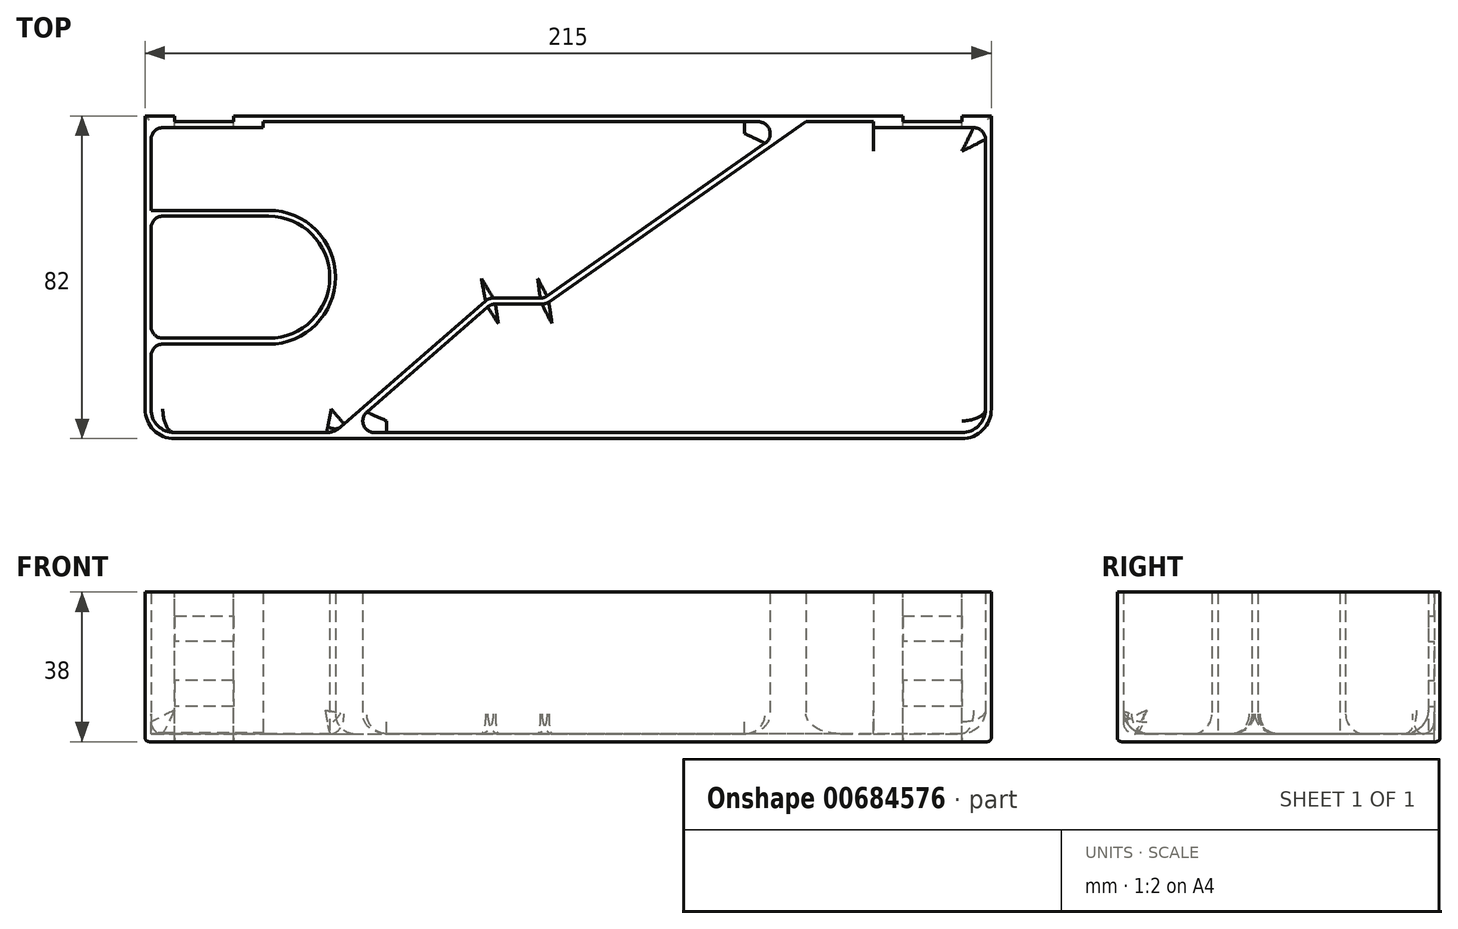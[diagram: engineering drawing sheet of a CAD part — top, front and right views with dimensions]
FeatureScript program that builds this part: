
annotation { "Feature Type Name" : "Feature", "Feature Type Description" : "" }
export const myFeature = defineFeature(function(context is Context, id is Id, definition is map)
    precondition{}
    {
        {
            var Q0;
            Q0=qCreatedBy(makeId("Top.planeOp"),FACE);
            var sketch = newSketch(context, id + "F0", { "sketchPlane" : qUnion([Q0])});
            skLineSegment(sketch, "E0.bottom", {"start": v(0, 0) * mm, "end": v(215, 0) * mm});
            skLineSegment(sketch, "E0.top", {"start": v(0, 82) * mm, "end": v(215, 82) * mm});
            skLineSegment(sketch, "E0.left", {"start": v(0, 0) * mm, "end": v(0, 82) * mm});
            skLineSegment(sketch, "E0.right", {"start": v(215, 0) * mm, "end": v(215, 82) * mm});
            skSolve(sketch);
        }
        {
            var Q0;
            Q0=makeQuery(id+"F0.imprint","IMPRINT",FACE,{"disambiguationData":[TD([[makeQuery(id+"F0.imprint","IMPRINT",EDGE,{"derivedFrom":sQuery(id+"F0.wireOp",EDGE,"E0.bottom")}),1.0]])]});
            extrude(context, id + "F1", {"entities" : qUnion([Q0]), "depth" : 2 * mm});
        }
        {
            var Q0;
            Q0=makeQuery(id+"F1.opExtrude","CAP_FACE",FACE,{"disambiguationData":[OSD([sQuery(id+"F0.wireOp",EDGE,"E0.bottom"),sQuery(id+"F0.wireOp",EDGE,"E0.top"),sQuery(id+"F0.wireOp",EDGE,"E0.left"),sQuery(id+"F0.wireOp",EDGE,"E0.right")])],"isStart":false});
            var sketch = newSketch(context, id + "F2", { "sketchPlane" : qUnion([Q0])});
            skLineSegment(sketch, "E1", {"start": v(1.5, 79) * mm, "end": v(30, 79) * mm});
            skLineSegment(sketch, "E2", {"start": v(30, 79) * mm, "end": v(30, 80.5) * mm});
            skLineSegment(sketch, "E3", {"start": v(30, 80.5) * mm, "end": v(185, 80.5) * mm});
            skLineSegment(sketch, "E4", {"start": v(185, 80.5) * mm, "end": v(185, 79) * mm});
            skLineSegment(sketch, "E5", {"start": v(185, 79) * mm, "end": v(213.5, 79) * mm});
            skLineSegment(sketch, "E6", {"start": v(213.5, 79) * mm, "end": v(213.5, 1.5) * mm});
            skLineSegment(sketch, "E7", {"start": v(213.5, 1.5) * mm, "end": v(1.5, 1.5) * mm});
            skLineSegment(sketch, "E8", {"start": v(1.5, 1.5) * mm, "end": v(1.5, 79) * mm});
            skSolve(sketch);
        }
        {
            var Q0;
            Q0=makeQuery(id+"F2.imprint","IMPRINT",FACE,{"disambiguationData":[TD([[makeQuery(id+"F2.imprint","IMPRINT",EDGE,{"derivedFrom":sQuery(id+"F2.wireOp",EDGE,"E1")}),1.0]])]});
            extrude(context, id + "F3", {"entities" : qUnion([Q0]), "operationType" : NewBodyOperationType.ADD, "depth" : 36 * mm});
        }
        {
            var Q0;
            Q0=makeQuery(id+"F1.opExtrude","CAP_FACE",FACE,{"disambiguationData":[OSD([sQuery(id+"F0.wireOp",EDGE,"E0.bottom"),sQuery(id+"F0.wireOp",EDGE,"E0.top"),sQuery(id+"F0.wireOp",EDGE,"E0.left"),sQuery(id+"F0.wireOp",EDGE,"E0.right")])],"isStart":false});
            var sketch = newSketch(context, id + "F4", { "sketchPlane" : qUnion([Q0])});
            skLineSegment(sketch, "E9", {"start": v(1.5, 58) * mm, "end": v(31.4, 58) * mm});
            skArc(sketch, "E10", {"start": v(31.4, 58) * mm, "mid": v(48.4, 41) * mm, "end": v(31.4, 24) * mm});
            skLineSegment(sketch, "E11", {"start": v(31.4, 24) * mm, "end": v(1.5, 24) * mm});
            skLineSegment(sketch, "E12", {"start": v(1.5, 24) * mm, "end": v(1.5, 25.5) * mm});
            skLineSegment(sketch, "E13", {"start": v(1.5, 25.5) * mm, "end": v(31.4, 25.5) * mm});
            skArc(sketch, "E14", {"start": v(31.4, 25.5) * mm, "mid": v(46.9, 41) * mm, "end": v(31.4, 56.5) * mm});
            skLineSegment(sketch, "E15", {"start": v(31.4, 56.5) * mm, "end": v(1.5, 56.5) * mm});
            skLineSegment(sketch, "E16", {"start": v(1.5, 56.5) * mm, "end": v(1.5, 58) * mm});
            skLineSegment(sketch, "E17", {"start": v(48, 1.5) * mm, "end": v(87.33, 35.69) * mm});
            skLineSegment(sketch, "E18", {"start": v(87.33, 35.69) * mm, "end": v(101.33, 35.69) * mm});
            skLineSegment(sketch, "E19", {"start": v(101.33, 35.69) * mm, "end": v(165.33, 80.5) * mm});
            skLineSegment(sketch, "E20", {"start": v(165.33, 80.5) * mm, "end": v(167.94, 80.5) * mm});
            skLineSegment(sketch, "E21", {"start": v(167.94, 80.5) * mm, "end": v(101.8, 34.19) * mm});
            skLineSegment(sketch, "E22", {"start": v(101.8, 34.19) * mm, "end": v(87.89, 34.19) * mm});
            skLineSegment(sketch, "E23", {"start": v(87.89, 34.19) * mm, "end": v(50.29, 1.5) * mm});
            skLineSegment(sketch, "E24", {"start": v(50.29, 1.5) * mm, "end": v(48, 1.5) * mm});
            skSolve(sketch);
        }
        {
            var Q0;
            Q0=makeQuery(id+"F4.imprint","IMPRINT",FACE,{"disambiguationData":[TD([[makeQuery(id+"F4.imprint","IMPRINT",EDGE,{"derivedFrom":sQuery(id+"F4.wireOp",EDGE,"E9")}),-1.0]])]});
            var Q1;
            Q1=makeQuery(id+"F4.imprint","IMPRINT",FACE,{"disambiguationData":[TD([[makeQuery(id+"F4.imprint","IMPRINT",EDGE,{"derivedFrom":sQuery(id+"F4.wireOp",EDGE,"E17")}),-1.0]])]});
            extrude(context, id + "F5", {"entities" : qUnion([Q0, Q1]), "operationType" : NewBodyOperationType.ADD, "depth" : 36 * mm});
        }
        {
            var Q0;
            Q0=makeQuery(id+"F1.opExtrude","CAP_EDGE",EDGE,{"disambiguationData":[OSD([sQuery(id+"F0.wireOp",EDGE,"E0.bottom")])],"isStart":true});
            var Q1;
            Q1=makeQuery(id+"F1.opExtrude","CAP_EDGE",EDGE,{"disambiguationData":[OSD([sQuery(id+"F0.wireOp",EDGE,"E0.right")])],"isStart":true});
            var Q2;
            Q2=makeQuery(id+"F1.opExtrude","CAP_EDGE",EDGE,{"disambiguationData":[OSD([sQuery(id+"F0.wireOp",EDGE,"E0.top")])],"isStart":true});
            var Q3;
            Q3=makeQuery(id+"F1.opExtrude","CAP_EDGE",EDGE,{"disambiguationData":[OSD([sQuery(id+"F0.wireOp",EDGE,"E0.left")])],"isStart":true});
            fillet(context, id + "F6", {"entities" : qUnion([Q0, Q1, Q2, Q3]), "radius" : 1 * mm, "tangentPropagation" : true, "allowEdgeOverflow" : false});
        }
        {
            var Q0;
            {var subQ0=sQuery(id+"F2.wireOp",EDGE,"E7");Q0=makeQuery(id+"F5.boolean.opBoolean","SPLIT",EDGE,{"disambiguationData":[TD([makeQuery(id+"F3.opExtrude","SWEPT_FACE",FACE,{"disambiguationData":[OSD([sQuery(id+"F2.wireOp",EDGE,"E6")])]})])],"derivedFrom":makeQuery(id+"F3.opExtrude","CAP_EDGE",EDGE,{"disambiguationData":[OSD([subQ0])],"isStart":true})});}
            var Q1;
            Q1=makeQuery(id+"F5.opExtrude","CAP_EDGE",EDGE,{"disambiguationData":[OSD([sQuery(id+"F4.wireOp",EDGE,"E23")])],"isStart":true});
            var Q2;
            Q2=makeQuery(id+"F5.opExtrude","CAP_EDGE",EDGE,{"disambiguationData":[OSD([sQuery(id+"F4.wireOp",EDGE,"E21")])],"isStart":true});
            var Q3;
            Q3=makeQuery(id+"F5.opExtrude","CAP_EDGE",EDGE,{"disambiguationData":[OSD([sQuery(id+"F4.wireOp",EDGE,"E22")])],"isStart":true});
            var Q4;
            {var subQ0=sQuery(id+"F2.wireOp",EDGE,"E3");Q4=makeQuery(id+"F5.boolean.opBoolean","SPLIT",EDGE,{"disambiguationData":[TD([makeQuery(id+"F3.opExtrude","SWEPT_FACE",FACE,{"disambiguationData":[OSD([sQuery(id+"F2.wireOp",EDGE,"E4")])]})])],"derivedFrom":makeQuery(id+"F3.opExtrude","CAP_EDGE",EDGE,{"disambiguationData":[OSD([subQ0])],"isStart":true})});}
            var Q5;
            Q5=makeQuery(id+"F3.opExtrude","CAP_EDGE",EDGE,{"disambiguationData":[OSD([sQuery(id+"F2.wireOp",EDGE,"E6")])],"isStart":true});
            var Q6;
            {var subQ0=sQuery(id+"F2.wireOp",EDGE,"E3");Q6=makeQuery(id+"F5.boolean.opBoolean","SPLIT",EDGE,{"disambiguationData":[TD([makeQuery(id+"F3.opExtrude","SWEPT_FACE",FACE,{"disambiguationData":[OSD([sQuery(id+"F2.wireOp",EDGE,"E2")])]})])],"derivedFrom":makeQuery(id+"F3.opExtrude","CAP_EDGE",EDGE,{"disambiguationData":[OSD([subQ0])],"isStart":true})});}
            var Q7;
            Q7=makeQuery(id+"F5.opExtrude","CAP_EDGE",EDGE,{"disambiguationData":[OSD([sQuery(id+"F4.wireOp",EDGE,"E19")])],"isStart":true});
            var Q8;
            Q8=makeQuery(id+"F5.opExtrude","CAP_EDGE",EDGE,{"disambiguationData":[OSD([sQuery(id+"F4.wireOp",EDGE,"E18")])],"isStart":true});
            var Q9;
            Q9=makeQuery(id+"F5.opExtrude","CAP_EDGE",EDGE,{"disambiguationData":[OSD([sQuery(id+"F4.wireOp",EDGE,"E17")])],"isStart":true});
            var Q10;
            {var subQ0=sQuery(id+"F2.wireOp",EDGE,"E8");Q10=makeQuery(id+"F5.boolean.opBoolean","SPLIT",EDGE,{"disambiguationData":[TD([makeQuery(id+"F3.opExtrude","SWEPT_FACE",FACE,{"disambiguationData":[OSD([sQuery(id+"F2.wireOp",EDGE,"E1")])]})])],"derivedFrom":makeQuery(id+"F3.opExtrude","CAP_EDGE",EDGE,{"disambiguationData":[OSD([subQ0])],"isStart":true})});}
            var Q11;
            Q11=makeQuery(id+"F5.opExtrude","CAP_EDGE",EDGE,{"disambiguationData":[OSD([sQuery(id+"F4.wireOp",EDGE,"E10")])],"isStart":true});
            var Q12;
            {var subQ0=sQuery(id+"F2.wireOp",EDGE,"E8");Q12=makeQuery(id+"F5.boolean.opBoolean","SPLIT",EDGE,{"disambiguationData":[TD([makeQuery(id+"F3.opExtrude","SWEPT_FACE",FACE,{"disambiguationData":[OSD([sQuery(id+"F2.wireOp",EDGE,"E7")])]})])],"derivedFrom":makeQuery(id+"F3.opExtrude","CAP_EDGE",EDGE,{"disambiguationData":[OSD([subQ0])],"isStart":true})});}
            var Q13;
            {var subQ0=sQuery(id+"F2.wireOp",EDGE,"E8");Q13=makeQuery(id+"F5.boolean.opBoolean","SPLIT",EDGE,{"disambiguationData":[TD([makeQuery(id+"F5.opExtrude","SWEPT_FACE",FACE,{"disambiguationData":[OSD([sQuery(id+"F4.wireOp",EDGE,"E13")])]})])],"derivedFrom":makeQuery(id+"F3.opExtrude","CAP_EDGE",EDGE,{"disambiguationData":[OSD([subQ0])],"isStart":true})});}
            var Q14;
            Q14=makeQuery(id+"F5.opExtrude","CAP_EDGE",EDGE,{"disambiguationData":[OSD([sQuery(id+"F4.wireOp",EDGE,"E15")])],"isStart":true});
            var Q15;
            {var subQ0=sQuery(id+"F2.wireOp",EDGE,"E7");Q15=makeQuery(id+"F5.boolean.opBoolean","SPLIT",EDGE,{"disambiguationData":[TD([makeQuery(id+"F3.opExtrude","SWEPT_FACE",FACE,{"disambiguationData":[OSD([sQuery(id+"F2.wireOp",EDGE,"E8")])]})])],"derivedFrom":makeQuery(id+"F3.opExtrude","CAP_EDGE",EDGE,{"disambiguationData":[OSD([subQ0])],"isStart":true})});}
            fillet(context, id + "F7", {"entities" : qUnion([Q0, Q1, Q2, Q3, Q4, Q5, Q6, Q7, Q8, Q9, Q10, Q11, Q12, Q13, Q14, Q15]), "radius" : 5 * mm, "tangentPropagation" : true, "allowEdgeOverflow" : false});
        }
        {
            var Q0;
            Q0=makeQuery(id+"F5.opExtrude","SWEPT_EDGE",EDGE,{"disambiguationData":[OSD([sQuery(id+"F2.wireOp",EDGE,"E7"),sQuery(id+"F4.wireOp",EDGE,"E17"),sQuery(id+"F4.wireOp",EDGE,"E24")])]});
            var Q1;
            Q1=makeQuery(id+"F5.opExtrude","SWEPT_EDGE",EDGE,{"disambiguationData":[OSD([sQuery(id+"F4.wireOp",EDGE,"E17"),sQuery(id+"F4.wireOp",EDGE,"E18")])]});
            var Q2;
            Q2=makeQuery(id+"F5.opExtrude","SWEPT_EDGE",EDGE,{"disambiguationData":[OSD([sQuery(id+"F4.wireOp",EDGE,"E18"),sQuery(id+"F4.wireOp",EDGE,"E19")])]});
            var Q3;
            Q3=makeQuery(id+"F5.opExtrude","SWEPT_EDGE",EDGE,{"disambiguationData":[OSD([sQuery(id+"F2.wireOp",EDGE,"E8"),sQuery(id+"F4.wireOp",EDGE,"E12"),sQuery(id+"F4.wireOp",EDGE,"E13")])]});
            var Q4;
            Q4=makeQuery(id+"F5.opExtrude","SWEPT_EDGE",EDGE,{"disambiguationData":[OSD([sQuery(id+"F2.wireOp",EDGE,"E8"),sQuery(id+"F4.wireOp",EDGE,"E9"),sQuery(id+"F4.wireOp",EDGE,"E16")])]});
            var Q5;
            Q5=makeQuery(id+"F5.opExtrude","SWEPT_EDGE",EDGE,{"disambiguationData":[OSD([sQuery(id+"F2.wireOp",EDGE,"E8"),sQuery(id+"F4.wireOp",EDGE,"E15"),sQuery(id+"F4.wireOp",EDGE,"E16")])]});
            var Q6;
            Q6=makeQuery(id+"F3.opExtrude","SWEPT_EDGE",EDGE,{"disambiguationData":[OSD([sQuery(id+"F2.wireOp",EDGE,"E1"),sQuery(id+"F2.wireOp",EDGE,"E8")])]});
            var Q7;
            Q7=makeQuery(id+"F5.opExtrude","SWEPT_EDGE",EDGE,{"disambiguationData":[OSD([sQuery(id+"F2.wireOp",EDGE,"E3"),sQuery(id+"F4.wireOp",EDGE,"E20"),sQuery(id+"F4.wireOp",EDGE,"E21")])]});
            var Q8;
            Q8=makeQuery(id+"F5.opExtrude","SWEPT_EDGE",EDGE,{"disambiguationData":[OSD([sQuery(id+"F2.wireOp",EDGE,"E3"),sQuery(id+"F4.wireOp",EDGE,"E19"),sQuery(id+"F4.wireOp",EDGE,"E20")])]});
            var Q9;
            Q9=makeQuery(id+"F3.opExtrude","SWEPT_EDGE",EDGE,{"disambiguationData":[OSD([sQuery(id+"F2.wireOp",EDGE,"E5"),sQuery(id+"F2.wireOp",EDGE,"E6")])]});
            var Q10;
            Q10=makeQuery(id+"F5.opExtrude","SWEPT_EDGE",EDGE,{"disambiguationData":[OSD([sQuery(id+"F2.wireOp",EDGE,"E7"),sQuery(id+"F4.wireOp",EDGE,"E23"),sQuery(id+"F4.wireOp",EDGE,"E24")])]});
            var Q11;
            Q11=makeQuery(id+"F5.opExtrude","SWEPT_EDGE",EDGE,{"disambiguationData":[OSD([sQuery(id+"F4.wireOp",EDGE,"E22"),sQuery(id+"F4.wireOp",EDGE,"E23")])]});
            var Q12;
            Q12=makeQuery(id+"F5.opExtrude","SWEPT_EDGE",EDGE,{"disambiguationData":[OSD([sQuery(id+"F4.wireOp",EDGE,"E21"),sQuery(id+"F4.wireOp",EDGE,"E22")])]});
            var Q13;
            Q13=makeQuery(id+"F5.opExtrude","SWEPT_EDGE",EDGE,{"disambiguationData":[OSD([sQuery(id+"F2.wireOp",EDGE,"E8"),sQuery(id+"F4.wireOp",EDGE,"E11"),sQuery(id+"F4.wireOp",EDGE,"E12")])]});
            fillet(context, id + "F8", {"entities" : qUnion([Q0, Q1, Q2, Q3, Q4, Q5, Q6, Q7, Q8, Q9, Q10, Q11, Q12, Q13]), "radius" : 3 * mm, "tangentPropagation" : true, "allowEdgeOverflow" : false});
        }
        {
            var Q0;
            Q0=makeQuery(id+"F3.opExtrude","SWEPT_EDGE",EDGE,{"disambiguationData":[OSD([sQuery(id+"F2.wireOp",EDGE,"E7"),sQuery(id+"F2.wireOp",EDGE,"E8")])]});
            var Q1;
            Q1=makeQuery(id+"F3.opExtrude","SWEPT_EDGE",EDGE,{"disambiguationData":[OSD([sQuery(id+"F2.wireOp",EDGE,"E6"),sQuery(id+"F2.wireOp",EDGE,"E7")])]});
            fillet(context, id + "F9", {"entities" : qUnion([Q0, Q1]), "radius" : 6 * mm, "tangentPropagation" : true, "allowEdgeOverflow" : false});
        }
        {
            var Q0;
            {var subQ0=sQuery(id+"F0.wireOp",EDGE,"E0.left");var subQ1=sQuery(id+"F0.wireOp",EDGE,"E0.bottom");Q0=makeQuery(id+"F3.boolean.opBoolean","MERGE",EDGE,{"derivedFrom":[makeQuery(id+"F1.opExtrude","SWEPT_EDGE",EDGE,{"disambiguationData":[OSD([subQ1,subQ0])]}),makeQuery(id+"F3.opExtrude","SWEPT_EDGE",EDGE,{"disambiguationData":[OSD([subQ1,subQ0])]})]});}
            var Q1;
            {var subQ0=sQuery(id+"F0.wireOp",EDGE,"E0.right");var subQ1=sQuery(id+"F0.wireOp",EDGE,"E0.bottom");Q1=makeQuery(id+"F3.boolean.opBoolean","MERGE",EDGE,{"derivedFrom":[makeQuery(id+"F1.opExtrude","SWEPT_EDGE",EDGE,{"disambiguationData":[OSD([subQ1,subQ0])]}),makeQuery(id+"F3.opExtrude","SWEPT_EDGE",EDGE,{"disambiguationData":[OSD([subQ1,subQ0])]})]});}
            fillet(context, id + "F10", {"entities" : qUnion([Q0, Q1]), "radius" : 7.5 * mm, "tangentPropagation" : true, "allowEdgeOverflow" : false});
        }
        {
            var Q0;
            Q0=makeQuery(id+"F5.boolean.opBoolean","MERGE",FACE,{"derivedFrom":[makeQuery(id+"F3.opExtrude","CAP_FACE",FACE,{"disambiguationData":[OSD([sQuery(id+"F0.wireOp",EDGE,"E0.bottom"),sQuery(id+"F0.wireOp",EDGE,"E0.top"),sQuery(id+"F0.wireOp",EDGE,"E0.left"),sQuery(id+"F0.wireOp",EDGE,"E0.right"),sQuery(id+"F2.wireOp",EDGE,"E1"),sQuery(id+"F2.wireOp",EDGE,"E2"),sQuery(id+"F2.wireOp",EDGE,"E3"),sQuery(id+"F2.wireOp",EDGE,"E4"),sQuery(id+"F2.wireOp",EDGE,"E5"),sQuery(id+"F2.wireOp",EDGE,"E6"),sQuery(id+"F2.wireOp",EDGE,"E7"),sQuery(id+"F2.wireOp",EDGE,"E8")])],"isStart":false}),makeQuery(id+"F5.opExtrude","CAP_FACE",FACE,{"disambiguationData":[OSD([sQuery(id+"F4.wireOp",EDGE,"E9"),sQuery(id+"F4.wireOp",EDGE,"E10"),sQuery(id+"F4.wireOp",EDGE,"E11"),sQuery(id+"F4.wireOp",EDGE,"E12"),sQuery(id+"F4.wireOp",EDGE,"E13"),sQuery(id+"F4.wireOp",EDGE,"E14"),sQuery(id+"F4.wireOp",EDGE,"E15"),sQuery(id+"F4.wireOp",EDGE,"E16")])],"isStart":false}),makeQuery(id+"F5.opExtrude","CAP_FACE",FACE,{"disambiguationData":[OSD([sQuery(id+"F4.wireOp",EDGE,"E17"),sQuery(id+"F4.wireOp",EDGE,"E18"),sQuery(id+"F4.wireOp",EDGE,"E19"),sQuery(id+"F4.wireOp",EDGE,"E20"),sQuery(id+"F4.wireOp",EDGE,"E21"),sQuery(id+"F4.wireOp",EDGE,"E22"),sQuery(id+"F4.wireOp",EDGE,"E23"),sQuery(id+"F4.wireOp",EDGE,"E24")])],"isStart":false})]});
            var sketch = newSketch(context, id + "F11", { "sketchPlane" : qUnion([Q0])});
            skLineSegment(sketch, "E25.bottom", {"start": v(7.5, 82) * mm, "end": v(22.5, 82) * mm});
            skLineSegment(sketch, "E25.top", {"start": v(7.5, 80.5) * mm, "end": v(22.5, 80.5) * mm});
            skLineSegment(sketch, "E25.left", {"start": v(7.5, 82) * mm, "end": v(7.5, 80.5) * mm});
            skLineSegment(sketch, "E25.right", {"start": v(22.5, 82) * mm, "end": v(22.5, 80.5) * mm});
            skLineSegment(sketch, "E26.bottom", {"start": v(192.5, 82) * mm, "end": v(207.5, 82) * mm});
            skLineSegment(sketch, "E26.top", {"start": v(192.5, 80.5) * mm, "end": v(207.5, 80.5) * mm});
            skLineSegment(sketch, "E26.left", {"start": v(192.5, 82) * mm, "end": v(192.5, 80.5) * mm});
            skLineSegment(sketch, "E26.right", {"start": v(207.5, 82) * mm, "end": v(207.5, 80.5) * mm});
            skSolve(sketch);
        }
        {
            var Q0;
            Q0=makeQuery(id+"F11.imprint","IMPRINT",FACE,{"disambiguationData":[TD([[makeQuery(id+"F11.imprint","IMPRINT",EDGE,{"derivedFrom":sQuery(id+"F11.wireOp",EDGE,"E26.bottom")}),-1.0]])]});
            var Q1;
            Q1=makeQuery(id+"F11.imprint","IMPRINT",FACE,{"disambiguationData":[TD([[makeQuery(id+"F11.imprint","IMPRINT",EDGE,{"derivedFrom":sQuery(id+"F11.wireOp",EDGE,"E25.bottom")}),-1.0]])]});
            extrude(context, id + "F12", {"entities" : qUnion([Q0, Q1]), "operationType" : NewBodyOperationType.REMOVE, "endBound" : BoundingType.THROUGH_ALL, "oppositeDirection" : true, "depth" : 25 * mm});
        }
        {
            var Q0;
            Q0=makeQuery(id+"F12.boolean.opBoolean","COPY",FACE,{"derivedFrom":makeQuery(id+"F12.opExtrude","SWEPT_FACE",FACE,{"disambiguationData":[OSD([sQuery(id+"F11.wireOp",EDGE,"E26.top")])]})});
            var sketch = newSketch(context, id + "F13", { "sketchPlane" : qUnion([Q0])});
            skLineSegment(sketch, "E27.bottom", {"start": v(-207.5, 32) * mm, "end": v(-192.5, 32) * mm});
            skLineSegment(sketch, "E27.top", {"start": v(-207.5, 25.5) * mm, "end": v(-192.5, 25.5) * mm});
            skLineSegment(sketch, "E27.left", {"start": v(-207.5, 32) * mm, "end": v(-207.5, 25.5) * mm});
            skLineSegment(sketch, "E27.right", {"start": v(-192.5, 32) * mm, "end": v(-192.5, 25.5) * mm});
            skLineSegment(sketch, "E28.bottom", {"start": v(-207.5, 15.5) * mm, "end": v(-192.5, 15.5) * mm});
            skLineSegment(sketch, "E28.top", {"start": v(-207.5, 9) * mm, "end": v(-192.5, 9) * mm});
            skLineSegment(sketch, "E28.left", {"start": v(-207.5, 15.5) * mm, "end": v(-207.5, 9) * mm});
            skLineSegment(sketch, "E28.right", {"start": v(-192.5, 15.5) * mm, "end": v(-192.5, 9) * mm});
            skSolve(sketch);
        }
        {
            var Q0;
            Q0=makeQuery(id+"F13.imprint","IMPRINT",FACE,{"disambiguationData":[TD([[makeQuery(id+"F13.imprint","IMPRINT",EDGE,{"derivedFrom":sQuery(id+"F13.wireOp",EDGE,"E27.bottom")}),-1.0]])]});
            var Q1;
            Q1=makeQuery(id+"F13.imprint","IMPRINT",FACE,{"disambiguationData":[TD([[makeQuery(id+"F13.imprint","IMPRINT",EDGE,{"derivedFrom":sQuery(id+"F13.wireOp",EDGE,"E28.bottom")}),-1.0]])]});
            extrude(context, id + "F14", {"entities" : qUnion([Q0, Q1]), "operationType" : NewBodyOperationType.REMOVE, "endBound" : BoundingType.UP_TO_NEXT, "oppositeDirection" : true, "depth" : 25 * mm});
        }
        {
            var Q0;
            Q0=makeQuery(id+"F12.boolean.opBoolean","COPY",FACE,{"derivedFrom":makeQuery(id+"F12.opExtrude","SWEPT_FACE",FACE,{"disambiguationData":[OSD([sQuery(id+"F11.wireOp",EDGE,"E25.top")])]})});
            var sketch = newSketch(context, id + "F15", { "sketchPlane" : qUnion([Q0])});
            skLineSegment(sketch, "E29.bottom", {"start": v(-22.5, 32) * mm, "end": v(-7.5, 32) * mm});
            skLineSegment(sketch, "E29.top", {"start": v(-22.5, 25.5) * mm, "end": v(-7.5, 25.5) * mm});
            skLineSegment(sketch, "E29.left", {"start": v(-22.5, 32) * mm, "end": v(-22.5, 25.5) * mm});
            skLineSegment(sketch, "E29.right", {"start": v(-7.5, 32) * mm, "end": v(-7.5, 25.5) * mm});
            skLineSegment(sketch, "E30.bottom", {"start": v(-22.5, 15.5) * mm, "end": v(-7.5, 15.5) * mm});
            skLineSegment(sketch, "E30.top", {"start": v(-22.5, 9) * mm, "end": v(-7.5, 9) * mm});
            skLineSegment(sketch, "E30.left", {"start": v(-22.5, 15.5) * mm, "end": v(-22.5, 9) * mm});
            skLineSegment(sketch, "E30.right", {"start": v(-7.5, 15.5) * mm, "end": v(-7.5, 9) * mm});
            skSolve(sketch);
        }
        {
            var Q0;
            Q0=makeQuery(id+"F15.imprint","IMPRINT",FACE,{"disambiguationData":[TD([[makeQuery(id+"F15.imprint","IMPRINT",EDGE,{"derivedFrom":sQuery(id+"F15.wireOp",EDGE,"E29.bottom")}),-1.0]])]});
            var Q1;
            Q1=makeQuery(id+"F15.imprint","IMPRINT",FACE,{"disambiguationData":[TD([[makeQuery(id+"F15.imprint","IMPRINT",EDGE,{"derivedFrom":sQuery(id+"F15.wireOp",EDGE,"E30.bottom")}),-1.0]])]});
            extrude(context, id + "F16", {"entities" : qUnion([Q0, Q1]), "operationType" : NewBodyOperationType.REMOVE, "endBound" : BoundingType.UP_TO_NEXT, "oppositeDirection" : true, "depth" : 25 * mm});
        }
    });
